# Revit family: Pump_Commercial-Submersible_Dewatering-Zoeller-76_Series
name_source: partatom
category: Mechanical Equipment
revit_build: Autodesk Revit 2014 (Build: 20130308_1515(x64)
units: mm (PartAtom-declared; Revit-internal decimal feet)

## types (1)
- M76
    Amps = 5 A
    Apparent Load = 575 VA
    Assembly Code = D2090
    Auto On/Off Points = 8-1/2in (21.6 cm) / 3-5/8in (9.2 cm)
    Base = Engineered Plastic
    Cooling = Oil free
    Cord Length = 9' (3 m) standard
    Cord Type = UL listed, 3-wire, cord and plug
    Default Elevation = 0"
    Description = Submersible pump for dewatering.
    Discharge Diameter = 1 1/2"
    Discharge Height = 3 3/4"
    Discharge Radius = 3/4"
    Flow @ 5' = 50 GPM
    Gasket = Buna-N o-ring
    Hardware = Stainless Steel
    Hertz = 60
    Horse Power = 1/2
    Impeller = Engineered Plastic
    Impeller Type = Non-clogging Vortex
    Installation Type = Floor Mounted
    Insulation = Class B
    Length = 9 1/16"
    Lower Bearing = Ball Bearing
    Manufacturer = Zoeller
    Max Flow Rate = 50 GPM (189 LPM)
    Max. Head = 25' (7.6 m)
    Max. Operating Temp. = 110° F (43° C)
    Mechanical Seals = Carbon/Ceramic
    Model = N76
    Motor Housing = Engineered Plastic
    Motor Protection = Auto reset thermal overload
    Motor Shaft = 410 Stainless Steel
    Operation = Automatic
    Overall Height = 12 5/8"
    Phase = 1 Ph
    Price = Prices may vary. Please consult Manufacturer Representative for most up-to-date price list.
    Product Documentation Link = http://cdn.qleapahead.com
    Product Page URL = http://www.zoellerpumps.com
    Pump Housing = Engineered Plastic
    RPM = 3400
    Solid Handling = 3/8in (9 mm) spherical solids
    Type = Permanent Split Capacitor
    URL = http://www.zoellerpumps.com
    Upper Bearing = Ball Bearing
    Voltage = 115 V
    Warranty Information = 36 Months (Limited)
    Waste Connection = Yes
    Width = 7 1/8"

## geometry (parser evidence)
native form markers: Sweep x3
no freeform markers — native parametric forms only
